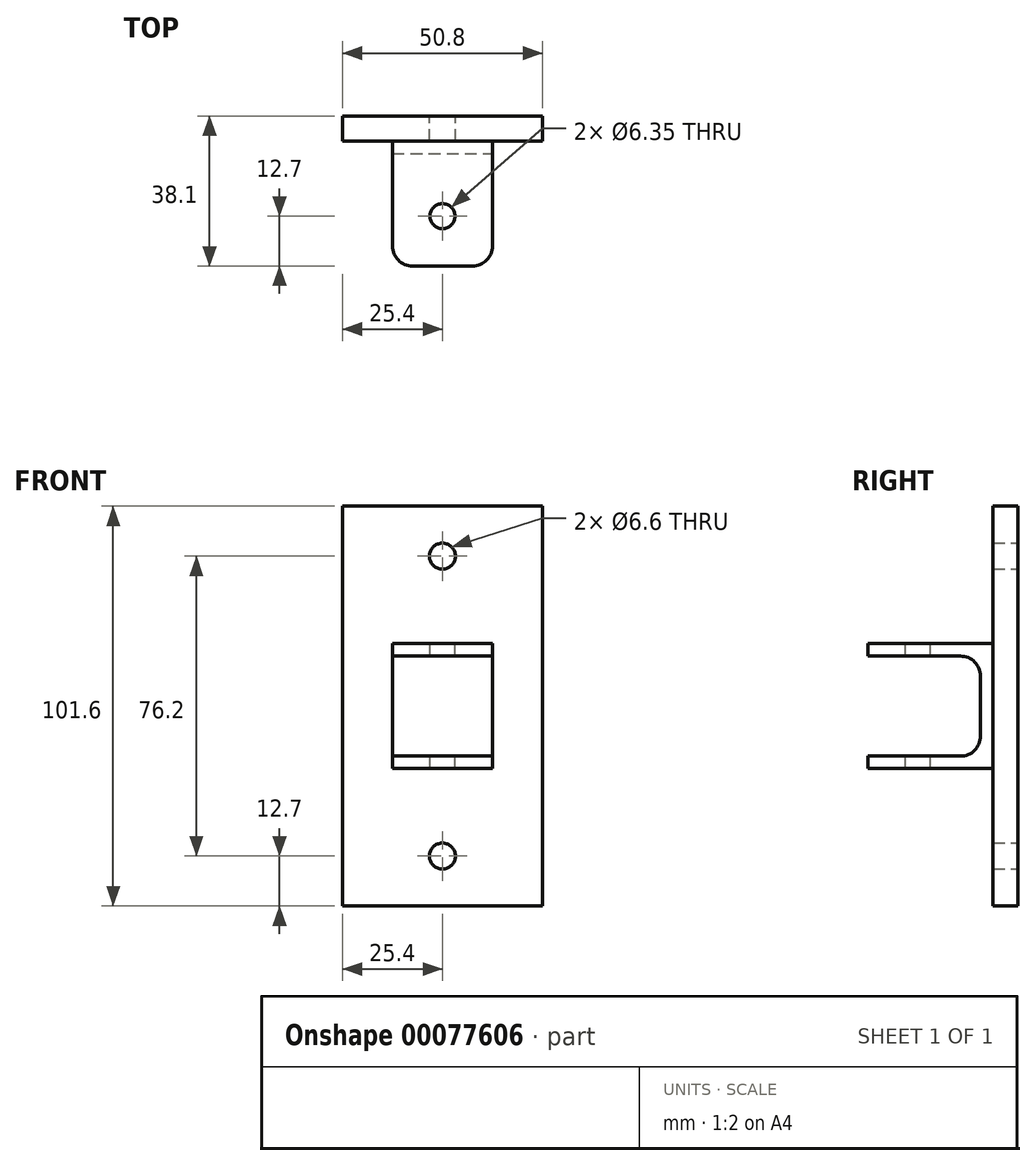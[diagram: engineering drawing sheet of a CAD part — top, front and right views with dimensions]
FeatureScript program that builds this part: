
annotation { "Feature Type Name" : "Feature", "Feature Type Description" : "" }
export const myFeature = defineFeature(function(context is Context, id is Id, definition is map)
    precondition{}
    {
        {
            var Q0;
            Q0=qCreatedBy(makeId("Front.planeOp"),FACE);
            var sketch = newSketch(context, id + "F0", { "sketchPlane" : qUnion([Q0])});
            skLineSegment(sketch, "E0.bottom", {"start": v(-25.4, 50.8) * mm, "end": v(25.4, 50.8) * mm});
            skLineSegment(sketch, "E0.top", {"start": v(-25.4, -50.8) * mm, "end": v(25.4, -50.8) * mm});
            skLineSegment(sketch, "E0.left", {"start": v(-25.4, 50.8) * mm, "end": v(-25.4, -50.8) * mm});
            skLineSegment(sketch, "E0.right", {"start": v(25.4, 50.8) * mm, "end": v(25.4, -50.8) * mm});
            skCircle(sketch, "E1", {"center": v(0, 38.1) * mm, "radius": 3.3 * mm});
            skPoint(sketch, "E1.centerSnap0", {"position": v(0, 50.8) * mm});
            skLineSegment(sketch, "E2", {"start": v(0, 0) * mm, "end": v(25.4, 0) * mm, "construction": true});
            skCircle(sketch, "E3.MirrorC", {"center": v(0, -38.1) * mm, "radius": 3.3 * mm});
            skSolve(sketch);
        }
        {
            var Q0;
            Q0 = qSketchRegion(id + "F0", true);
            extrude(context, id + "F1", {"entities" : qUnion([Q0]), "depth" : 6.35 * mm});
        }
        {
            var Q0;
            Q0=makeQuery(id+"F1.opExtrude","CAP_FACE",FACE,{"disambiguationData":[OSD([sQuery(id+"F0.wireOp",EDGE,"E0.bottom"),sQuery(id+"F0.wireOp",EDGE,"E0.top"),sQuery(id+"F0.wireOp",EDGE,"E0.left"),sQuery(id+"F0.wireOp",EDGE,"E0.right"),sQuery(id+"F0.wireOp",EDGE,"E1"),sQuery(id+"F0.wireOp",EDGE,"E3.MirrorC")])],"isStart":false});
            var sketch = newSketch(context, id + "F2", { "sketchPlane" : qUnion([Q0])});
            skLineSegment(sketch, "E4.bottom", {"start": v(-12.7, 12.7) * mm, "end": v(12.7, 12.7) * mm});
            skLineSegment(sketch, "E4.top", {"start": v(-12.7, -12.7) * mm, "end": v(12.7, -12.7) * mm});
            skLineSegment(sketch, "E4.left", {"start": v(-12.7, 12.7) * mm, "end": v(-12.7, -12.7) * mm});
            skLineSegment(sketch, "E4.right", {"start": v(12.7, 12.7) * mm, "end": v(12.7, -12.7) * mm});
            skLineSegment(sketch, "E5.top", {"start": v(-12.7, 15.87) * mm, "end": v(12.7, 15.87) * mm});
            skLineSegment(sketch, "E5.left", {"start": v(-12.7, 12.7) * mm, "end": v(-12.7, 15.87) * mm});
            skLineSegment(sketch, "E5.right", {"start": v(12.7, 12.7) * mm, "end": v(12.7, 15.87) * mm});
            skLineSegment(sketch, "E6.top", {"start": v(-12.7, -15.88) * mm, "end": v(12.7, -15.88) * mm});
            skLineSegment(sketch, "E6.left", {"start": v(-12.7, -12.7) * mm, "end": v(-12.7, -15.88) * mm});
            skLineSegment(sketch, "E6.right", {"start": v(12.7, -12.7) * mm, "end": v(12.7, -15.88) * mm});
            skSolve(sketch);
        }
        {
            var Q0;
            Q0=makeQuery(id+"F2.imprint","IMPRINT",FACE,{"disambiguationData":[TD([[makeQuery(id+"F2.imprint","IMPRINT",EDGE,{"derivedFrom":sQuery(id+"F2.wireOp",EDGE,"E4.top")}),-1.0]])]});
            var Q1;
            Q1=makeQuery(id+"F2.imprint","IMPRINT",FACE,{"disambiguationData":[TD([[makeQuery(id+"F2.imprint","IMPRINT",EDGE,{"derivedFrom":sQuery(id+"F2.wireOp",EDGE,"E4.bottom")}),1.0]])]});
            extrude(context, id + "F3", {"entities" : qUnion([Q0, Q1]), "operationType" : NewBodyOperationType.ADD, "depth" : 31.75 * mm});
        }
        {
            var Q0;
            Q0 = qSketchRegion(id + "F2", true);
            extrude(context, id + "F4", {"entities" : qUnion([Q0]), "operationType" : NewBodyOperationType.ADD, "depth" : 3.17 * mm});
        }
        {
            var Q0;
            Q0=makeQuery(id+"F4.boolean.opBoolean","INTERSECT",EDGE,{"derivedFrom":[makeQuery(id+"F3.opExtrude","SWEPT_FACE",FACE,{"disambiguationData":[OSD([sQuery(id+"F2.wireOp",EDGE,"E4.top")])]}),makeQuery(id+"F4.opExtrude","CAP_FACE",FACE,{"disambiguationData":[OSD([sQuery(id+"F2.wireOp",EDGE,"E4.left"),sQuery(id+"F2.wireOp",EDGE,"E4.right"),sQuery(id+"F2.wireOp",EDGE,"E5.top"),sQuery(id+"F2.wireOp",EDGE,"E5.left"),sQuery(id+"F2.wireOp",EDGE,"E5.right"),sQuery(id+"F2.wireOp",EDGE,"E6.top"),sQuery(id+"F2.wireOp",EDGE,"E6.left"),sQuery(id+"F2.wireOp",EDGE,"E6.right")])],"isStart":false})]});
            var Q1;
            Q1=makeQuery(id+"F4.boolean.opBoolean","INTERSECT",EDGE,{"derivedFrom":[makeQuery(id+"F3.opExtrude","SWEPT_FACE",FACE,{"disambiguationData":[OSD([sQuery(id+"F2.wireOp",EDGE,"E4.bottom")])]}),makeQuery(id+"F4.opExtrude","CAP_FACE",FACE,{"disambiguationData":[OSD([sQuery(id+"F2.wireOp",EDGE,"E4.left"),sQuery(id+"F2.wireOp",EDGE,"E4.right"),sQuery(id+"F2.wireOp",EDGE,"E5.top"),sQuery(id+"F2.wireOp",EDGE,"E5.left"),sQuery(id+"F2.wireOp",EDGE,"E5.right"),sQuery(id+"F2.wireOp",EDGE,"E6.top"),sQuery(id+"F2.wireOp",EDGE,"E6.left"),sQuery(id+"F2.wireOp",EDGE,"E6.right")])],"isStart":false})]});
            fillet(context, id + "F5", {"entities" : qUnion([Q0, Q1]), "radius" : 5.08 * mm, "tangentPropagation" : true, "allowEdgeOverflow" : false});
        }
        {
            var Q0;
            Q0=makeQuery(id+"F3.opExtrude","CAP_EDGE",EDGE,{"disambiguationData":[OSD([sQuery(id+"F2.wireOp",EDGE,"E5.right")])],"isStart":false});
            var Q1;
            Q1=makeQuery(id+"F3.opExtrude","CAP_EDGE",EDGE,{"disambiguationData":[OSD([sQuery(id+"F2.wireOp",EDGE,"E5.left")])],"isStart":false});
            var Q2;
            Q2=makeQuery(id+"F3.opExtrude","CAP_EDGE",EDGE,{"disambiguationData":[OSD([sQuery(id+"F2.wireOp",EDGE,"E6.right")])],"isStart":false});
            var Q3;
            Q3=makeQuery(id+"F3.opExtrude","CAP_EDGE",EDGE,{"disambiguationData":[OSD([sQuery(id+"F2.wireOp",EDGE,"E6.left")])],"isStart":false});
            fillet(context, id + "F6", {"entities" : qUnion([Q0, Q1, Q2, Q3]), "radius" : 5.08 * mm, "tangentPropagation" : true, "allowEdgeOverflow" : false});
        }
        {
            var Q0;
            Q0=makeQuery(id+"F3.opExtrude","SWEPT_FACE",FACE,{"disambiguationData":[OSD([sQuery(id+"F2.wireOp",EDGE,"E5.top")])]});
            var sketch = newSketch(context, id + "F7", { "sketchPlane" : qUnion([Q0])});
            skCircle(sketch, "E7", {"center": v(0, -25.4) * mm, "radius": 3.18 * mm});
            skSolve(sketch);
        }
        {
            var Q0;
            Q0 = qSketchRegion(id + "F7", true);
            extrude(context, id + "F8", {"entities" : qUnion([Q0]), "operationType" : NewBodyOperationType.REMOVE, "endBound" : BoundingType.THROUGH_ALL, "oppositeDirection" : true, "depth" : 25.4 * mm});
        }
    });
